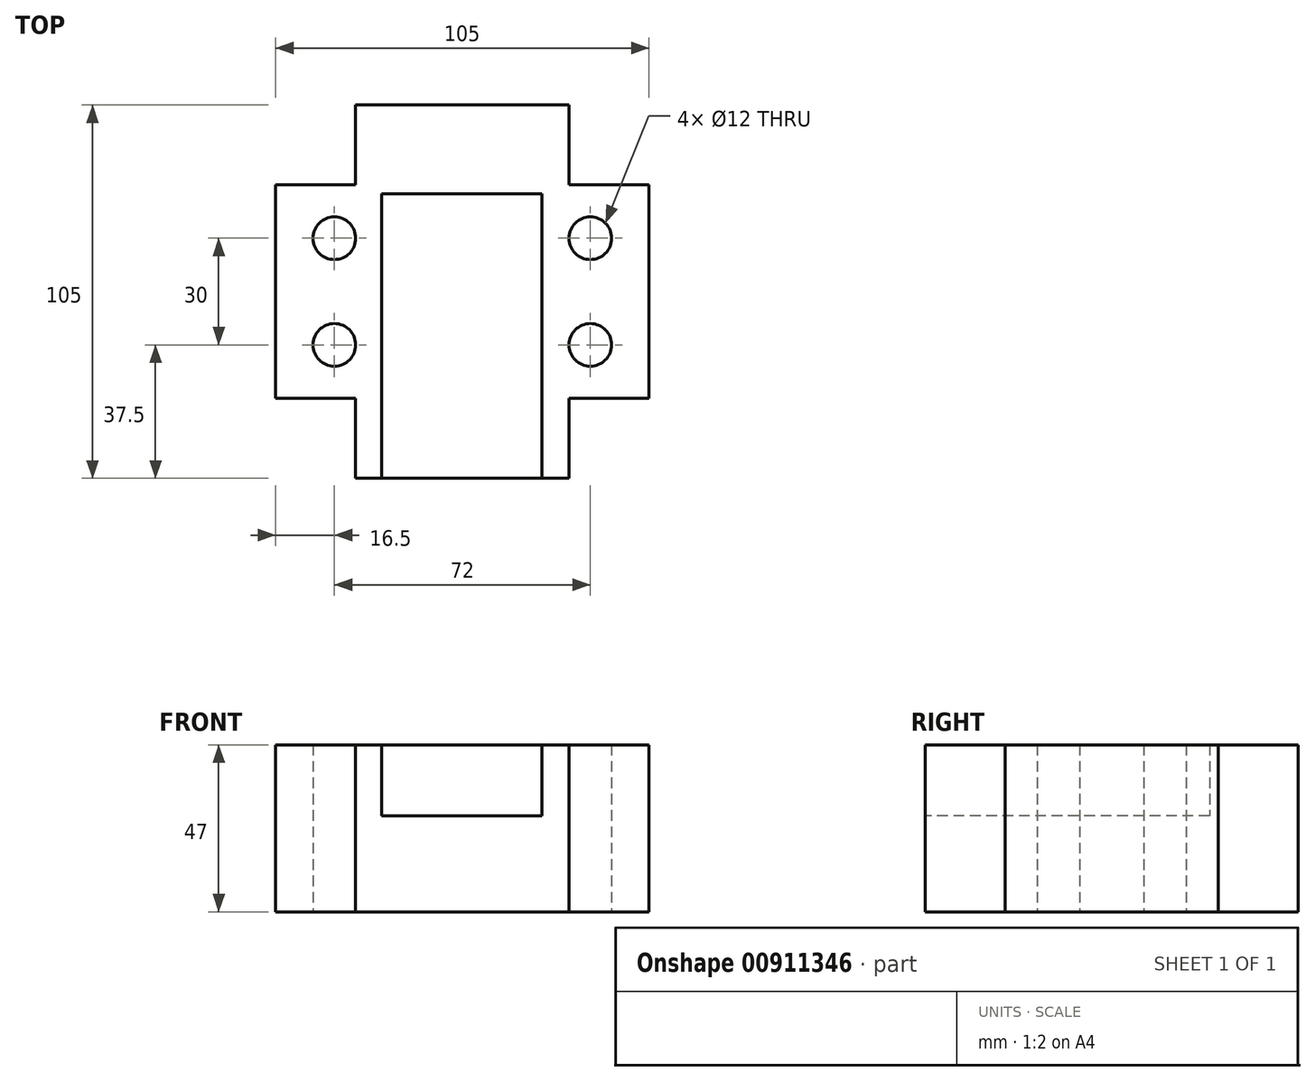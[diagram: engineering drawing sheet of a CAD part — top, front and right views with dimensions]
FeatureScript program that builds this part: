
annotation { "Feature Type Name" : "Feature", "Feature Type Description" : "" }
export const myFeature = defineFeature(function(context is Context, id is Id, definition is map)
    precondition{}
    {
        {
            var Q0;
            Q0=qCreatedBy(makeId("Top.planeOp"),FACE);
            var sketch = newSketch(context, id + "F0", { "sketchPlane" : qUnion([Q0])});
            skLineSegment(sketch, "E0.bottom", {"start": v(30, 52.5) * mm, "end": v(-30, 52.5) * mm});
            skLineSegment(sketch, "E0.top", {"start": v(30, -52.5) * mm, "end": v(-30, -52.5) * mm});
            skLineSegment(sketch, "E0.left", {"start": v(52.5, 30) * mm, "end": v(52.5, -30) * mm});
            skLineSegment(sketch, "E0.right", {"start": v(-52.5, 30) * mm, "end": v(-52.5, -30) * mm});
            skPoint(sketch, "E0.middle", {"position": v(0, 0) * mm});
            skLineSegment(sketch, "E1", {"start": v(-52.5, 30) * mm, "end": v(-30, 30) * mm});
            skLineSegment(sketch, "E2", {"start": v(-30, 30) * mm, "end": v(-30, 52.5) * mm});
            skPoint(sketch, "E3.orphan", {"position": v(-52.5, 52.5) * mm});
            skLineSegment(sketch, "E4.MirrorCS", {"start": v(-52.5, -30) * mm, "end": v(-30, -30) * mm});
            skLineSegment(sketch, "E5.MirrorCS", {"start": v(-30, -30) * mm, "end": v(-30, -52.5) * mm});
            skPoint(sketch, "E6.orphan", {"position": v(-52.5, -52.5) * mm});
            skLineSegment(sketch, "E7.MirrorCS", {"start": v(30, 30) * mm, "end": v(30, 52.5) * mm});
            skLineSegment(sketch, "E8.MirrorCS", {"start": v(52.5, 30) * mm, "end": v(30, 30) * mm});
            skLineSegment(sketch, "E9.MirrorCS", {"start": v(52.5, -30) * mm, "end": v(30, -30) * mm});
            skLineSegment(sketch, "E10.MirrorCS", {"start": v(30, -30) * mm, "end": v(30, -52.5) * mm});
            skPoint(sketch, "E11.orphan", {"position": v(52.5, 52.5) * mm});
            skPoint(sketch, "E12.orphan", {"position": v(52.5, -52.5) * mm});
            skCircle(sketch, "E13", {"center": v(-36, 15) * mm, "radius": 6 * mm});
            skCircle(sketch, "E14.MirrorC", {"center": v(36, 15) * mm, "radius": 6 * mm});
            skCircle(sketch, "E15.MirrorC", {"center": v(-36, -15) * mm, "radius": 6 * mm});
            skCircle(sketch, "E16.MirrorC", {"center": v(36, -15) * mm, "radius": 6 * mm});
            skSolve(sketch);
        }
        {
            var Q0;
            Q0 = qSketchRegion(id + "F0", true);
            extrude(context, id + "F1", {"entities" : qUnion([Q0]), "depth" : 35 * mm, "offsetDistance" : 25 * mm, "hasSecondDirection" : true, "secondDirectionOppositeDirection" : true, "secondDirectionDepth" : 12 * mm});
        }
        {
            var Q0;
            Q0=makeQuery(id+"F1.opExtrude","SWEPT_FACE",FACE,{"disambiguationData":[OSD([sQuery(id+"F0.wireOp",EDGE,"E0.top")])]});
            var sketch = newSketch(context, id + "F2", { "sketchPlane" : qUnion([Q0])});
            skLineSegment(sketch, "E17.bottom", {"start": v(-22.63, 35) * mm, "end": v(22.37, 35) * mm});
            skLineSegment(sketch, "E17.top", {"start": v(-22.63, 15) * mm, "end": v(22.37, 15) * mm});
            skLineSegment(sketch, "E17.left", {"start": v(-22.63, 35) * mm, "end": v(-22.63, 15) * mm});
            skLineSegment(sketch, "E17.right", {"start": v(22.37, 35) * mm, "end": v(22.37, 15) * mm});
            skLineSegment(sketch, "E18.MirrorCS", {"start": v(22.63, 35) * mm, "end": v(22.63, 15) * mm});
            skSolve(sketch);
        }
        {
            var Q0;
            Q0=makeQuery(id+"F2.imprint","IMPRINT",FACE,{"disambiguationData":[TD([[makeQuery(id+"F2.imprint","IMPRINT",EDGE,{"derivedFrom":sQuery(id+"F2.wireOp",EDGE,"E17.bottom")}),1.0]])]});
            extrude(context, id + "F3", {"entities" : qUnion([Q0]), "operationType" : NewBodyOperationType.REMOVE, "oppositeDirection" : true, "depth" : 80 * mm, "offsetDistance" : 25 * mm});
        }
    });
